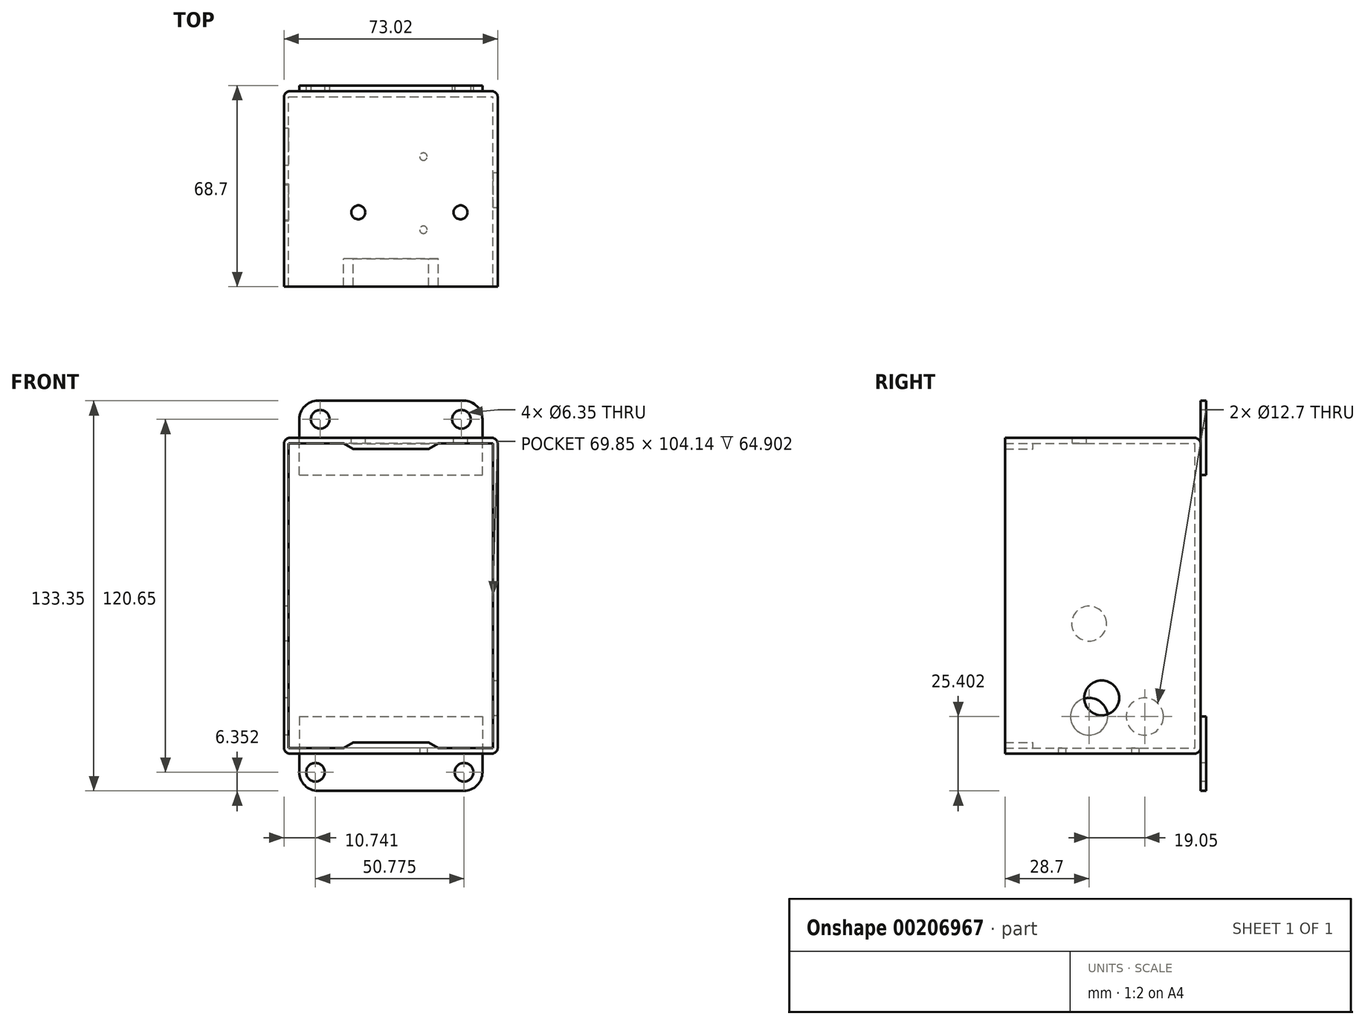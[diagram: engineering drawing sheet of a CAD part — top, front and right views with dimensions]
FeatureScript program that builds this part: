
annotation { "Feature Type Name" : "Feature", "Feature Type Description" : "" }
export const myFeature = defineFeature(function(context is Context, id is Id, definition is map)
    precondition{}
    {
        {
            var Q0;
            Q0=qCreatedBy(makeId("Front.planeOp"),FACE);
            var sketch = newSketch(context, id + "F0", { "sketchPlane" : qUnion([Q0])});
            skLineSegment(sketch, "E0", {"start": v(-80.79, 134.9) * mm, "end": v(-131.65, 134.9) * mm});
            skLineSegment(sketch, "E1", {"start": v(-74.44, 125.38) * mm, "end": v(-74.44, 128.55) * mm});
            skLineSegment(sketch, "E2", {"start": v(-138, 125.38) * mm, "end": v(-138, 128.55) * mm});
            skCircle(sketch, "E3", {"center": v(-81.58, 128.55) * mm, "radius": 3.18 * mm});
            skCircle(sketch, "E4", {"center": v(-130.86, 128.55) * mm, "radius": 3.18 * mm});
            skArc(sketch, "E5", {"start": v(-74.44, 128.55) * mm, "mid": v(-76.3, 133.04) * mm, "end": v(-80.79, 134.9) * mm});
            skArc(sketch, "E6", {"start": v(-131.65, 134.9) * mm, "mid": v(-136.14, 133.04) * mm, "end": v(-138, 128.55) * mm});
            skArc(sketch, "E7", {"start": v(-138, 7.9) * mm, "mid": v(-136.14, 3.41) * mm, "end": v(-131.65, 1.55) * mm});
            skArc(sketch, "E8", {"start": v(-80.79, 1.55) * mm, "mid": v(-76.3, 3.41) * mm, "end": v(-74.44, 7.9) * mm});
            skCircle(sketch, "E9", {"center": v(-130.86, 7.9) * mm, "radius": 3.18 * mm});
            skCircle(sketch, "E10", {"center": v(-81.58, 7.9) * mm, "radius": 3.18 * mm});
            skLineSegment(sketch, "E11", {"start": v(-138, 11.08) * mm, "end": v(-138, 7.9) * mm});
            skLineSegment(sketch, "E12", {"start": v(-74.44, 11.08) * mm, "end": v(-74.44, 7.9) * mm});
            skLineSegment(sketch, "E13", {"start": v(-80.79, 1.55) * mm, "end": v(-131.65, 1.55) * mm});
            skLineSegment(sketch, "E14", {"start": v(-141.97, -160.1) * mm, "end": v(-70.47, -160.1) * mm});
            skLineSegment(sketch, "E15", {"start": v(-141.97, -98.67) * mm, "end": v(-141.97, -160.1) * mm});
            skLineSegment(sketch, "E16", {"start": v(-70.47, -98.67) * mm, "end": v(-70.47, -160.1) * mm});
            skLineSegment(sketch, "E17", {"start": v(-74.44, -160.1) * mm, "end": v(-74.44, -162.01) * mm});
            skLineSegment(sketch, "E18", {"start": v(-138, -160.1) * mm, "end": v(-138, -162.01) * mm});
            skLineSegment(sketch, "E19", {"start": v(-138, -162.01) * mm, "end": v(-74.44, -162.01) * mm});
            skLineSegment(sketch, "E20", {"start": v(-119.33, -98.67) * mm, "end": v(-119.33, -104.55) * mm});
            skLineSegment(sketch, "E21", {"start": v(-93.1, -98.67) * mm, "end": v(-93.1, -104.55) * mm});
            skLineSegment(sketch, "E22", {"start": v(-119.33, -104.55) * mm, "end": v(-93.1, -104.55) * mm});
            skLineSegment(sketch, "E23", {"start": v(-143.69, -89.15) * mm, "end": v(-68.75, -89.15) * mm});
            skLineSegment(sketch, "E24", {"start": v(-145.98, -98.67) * mm, "end": v(-66.46, -98.67) * mm});
            skLineSegment(sketch, "E25", {"start": v(-67.17, -90.6) * mm, "end": v(-66.46, -98.67) * mm});
            skLineSegment(sketch, "E26", {"start": v(-145.27, -90.6) * mm, "end": v(-145.98, -98.67) * mm});
            skArc(sketch, "E27", {"start": v(-67.17, -90.6) * mm, "mid": v(-67.67, -89.57) * mm, "end": v(-68.75, -89.15) * mm});
            skArc(sketch, "E28", {"start": v(-143.69, -89.15) * mm, "mid": v(-144.76, -89.57) * mm, "end": v(-145.27, -90.6) * mm});
            skLineSegment(sketch, "E29", {"start": v(-106.22, -87.6) * mm, "end": v(-105.17, -87.6) * mm});
            skArc(sketch, "E30", {"start": v(-101.46, -89.15) * mm, "mid": v(-103, -87.36) * mm, "end": v(-105.17, -86.4) * mm});
            skLineSegment(sketch, "E31", {"start": v(-105.17, -87.6) * mm, "end": v(-105.17, -86.4) * mm});
            skLineSegment(sketch, "E32", {"start": v(-106.22, -87.6) * mm, "end": v(-107.27, -87.6) * mm});
            skLineSegment(sketch, "E33", {"start": v(-107.27, -87.6) * mm, "end": v(-107.27, -86.4) * mm});
            skArc(sketch, "E34", {"start": v(-107.27, -86.4) * mm, "mid": v(-109.43, -87.36) * mm, "end": v(-110.98, -89.15) * mm});
            skLineSegment(sketch, "E35", {"start": v(-66.46, 14.25) * mm, "end": v(-66.46, 122.2) * mm});
            skLineSegment(sketch, "E36", {"start": v(-145.98, 14.25) * mm, "end": v(-145.98, 122.2) * mm});
            skLineSegment(sketch, "E37", {"start": v(-69.63, 125.38) * mm, "end": v(-142.8, 125.38) * mm});
            skLineSegment(sketch, "E38", {"start": v(-69.63, 11.08) * mm, "end": v(-142.8, 11.08) * mm});
            skArc(sketch, "E39", {"start": v(6.1, 134.9) * mm, "mid": v(1.6, 133.04) * mm, "end": v(-0.25, 128.55) * mm});
            skArc(sketch, "E40", {"start": v(62.3, 128.55) * mm, "mid": v(60.43, 133.04) * mm, "end": v(55.94, 134.9) * mm});
            skCircle(sketch, "E41", {"center": v(6.89, 128.55) * mm, "radius": 3.18 * mm});
            skCircle(sketch, "E42", {"center": v(55.15, 128.55) * mm, "radius": 3.18 * mm});
            skLineSegment(sketch, "E43", {"start": v(55.94, 1.55) * mm, "end": v(6.1, 1.55) * mm});
            skLineSegment(sketch, "E44", {"start": v(67.53, 14.25) * mm, "end": v(62.3, 14.25) * mm});
            skLineSegment(sketch, "E45", {"start": v(65.94, 16.16) * mm, "end": v(47.21, 16.16) * mm});
            skLineSegment(sketch, "E46", {"start": v(65.94, 120.3) * mm, "end": v(47.21, 120.3) * mm});
            skLineSegment(sketch, "E47", {"start": v(-5.5, 14.25) * mm, "end": v(-5.5, 122.2) * mm});
            skLineSegment(sketch, "E48", {"start": v(-3.9, 16.16) * mm, "end": v(-3.9, 120.3) * mm});
            skCircle(sketch, "E49", {"center": v(5.25, 7.9) * mm, "radius": 3.18 * mm});
            skArc(sketch, "E50", {"start": v(-0.25, 7.9) * mm, "mid": v(1.6, 3.41) * mm, "end": v(6.1, 1.55) * mm});
            skLineSegment(sketch, "E51", {"start": v(-3.9, 16.16) * mm, "end": v(14.83, 16.16) * mm});
            skLineSegment(sketch, "E52", {"start": v(-5.5, 14.25) * mm, "end": v(-0.25, 14.25) * mm});
            skLineSegment(sketch, "E53", {"start": v(-0.25, 14.25) * mm, "end": v(-0.25, 7.9) * mm});
            skLineSegment(sketch, "E54", {"start": v(14.83, 16.16) * mm, "end": v(18.13, 18.06) * mm});
            skLineSegment(sketch, "E55", {"start": v(-0.25, 14.25) * mm, "end": v(62.3, 14.25) * mm});
            skLineSegment(sketch, "E56", {"start": v(18.13, 18.06) * mm, "end": v(43.91, 18.06) * mm});
            skLineSegment(sketch, "E57", {"start": v(47.21, 16.16) * mm, "end": v(43.91, 18.06) * mm});
            skLineSegment(sketch, "E58", {"start": v(62.3, 122.2) * mm, "end": v(67.53, 122.2) * mm});
            skLineSegment(sketch, "E59", {"start": v(-3.9, 120.3) * mm, "end": v(14.83, 120.3) * mm});
            skLineSegment(sketch, "E60", {"start": v(-0.25, 122.2) * mm, "end": v(-0.25, 128.55) * mm});
            skLineSegment(sketch, "E61", {"start": v(14.83, 120.3) * mm, "end": v(18.13, 118.4) * mm});
            skLineSegment(sketch, "E62", {"start": v(18.13, 118.4) * mm, "end": v(43.91, 118.4) * mm});
            skLineSegment(sketch, "E63", {"start": v(47.21, 120.3) * mm, "end": v(43.91, 118.4) * mm});
            skLineSegment(sketch, "E64", {"start": v(67.53, 122.2) * mm, "end": v(67.53, 14.25) * mm});
            skLineSegment(sketch, "E65", {"start": v(65.94, 120.3) * mm, "end": v(65.94, 16.16) * mm});
            skArc(sketch, "E66", {"start": v(55.94, 1.55) * mm, "mid": v(60.43, 3.41) * mm, "end": v(62.3, 7.9) * mm});
            skLineSegment(sketch, "E67", {"start": v(62.3, 14.25) * mm, "end": v(62.3, 7.9) * mm});
            skCircle(sketch, "E68", {"center": v(56.03, 7.9) * mm, "radius": 3.18 * mm});
            skLineSegment(sketch, "E69", {"start": v(62.3, 122.2) * mm, "end": v(62.3, 128.55) * mm});
            skLineSegment(sketch, "E70", {"start": v(55.94, 134.9) * mm, "end": v(6.1, 134.9) * mm});
            skCircle(sketch, "E71", {"center": v(-106.22, 119.28) * mm, "radius": 4.76 * mm});
            skCircle(sketch, "E72", {"center": v(-106.22, 18.19) * mm, "radius": 4.76 * mm});
            skLineSegment(sketch, "E73", {"start": v(-105.17, 13.54) * mm, "end": v(-105.17, 22.83) * mm});
            skLineSegment(sketch, "E74", {"start": v(-107.27, 13.54) * mm, "end": v(-107.27, 22.83) * mm});
            skLineSegment(sketch, "E75", {"start": v(-110.49, 121.4) * mm, "end": v(-103.27, 115.54) * mm});
            skLineSegment(sketch, "E76", {"start": v(-109.17, 123.02) * mm, "end": v(-101.95, 117.17) * mm});
            skArc(sketch, "E77", {"start": v(-66.46, 122.2) * mm, "mid": v(-67.39, 124.45) * mm, "end": v(-69.63, 125.38) * mm});
            skArc(sketch, "E78", {"start": v(-142.8, 125.38) * mm, "mid": v(-145.05, 124.45) * mm, "end": v(-145.98, 122.2) * mm});
            skArc(sketch, "E79", {"start": v(-145.98, 14.25) * mm, "mid": v(-145.05, 12) * mm, "end": v(-142.8, 11.08) * mm});
            skArc(sketch, "E80", {"start": v(-69.63, 11.08) * mm, "mid": v(-67.39, 12) * mm, "end": v(-66.46, 14.25) * mm});
            skLineSegment(sketch, "E81", {"start": v(-141.97, -93.43) * mm, "end": v(-70.47, -93.43) * mm});
            skLineSegment(sketch, "E82", {"start": v(-141.97, -93.43) * mm, "end": v(-141.97, -98.67) * mm});
            skLineSegment(sketch, "E83", {"start": v(-70.47, -98.67) * mm, "end": v(-70.47, -93.43) * mm});
            skLineSegment(sketch, "E84", {"start": v(-72.37, -98.67) * mm, "end": v(-72.37, -158.2) * mm});
            skLineSegment(sketch, "E85", {"start": v(-140.06, -158.2) * mm, "end": v(-72.37, -158.2) * mm});
            skLineSegment(sketch, "E86", {"start": v(-140.06, -98.67) * mm, "end": v(-140.06, -158.2) * mm});
            skLineSegment(sketch, "E87", {"start": v(-140.06, -93.43) * mm, "end": v(-140.06, -98.67) * mm});
            skLineSegment(sketch, "E88", {"start": v(-72.37, -98.67) * mm, "end": v(-72.37, -93.43) * mm});
            skLineSegment(sketch, "E89", {"start": v(-86.66, 128.55) * mm, "end": v(-76.5, 128.55) * mm});
            skLineSegment(sketch, "E90", {"start": v(-81.58, 133.63) * mm, "end": v(-81.58, 123.47) * mm});
            skLineSegment(sketch, "E91", {"start": v(-135.94, 128.55) * mm, "end": v(-125.78, 128.55) * mm});
            skLineSegment(sketch, "E92", {"start": v(-130.86, 133.63) * mm, "end": v(-130.86, 123.47) * mm});
            skLineSegment(sketch, "E93", {"start": v(-135.94, 7.9) * mm, "end": v(-125.78, 7.9) * mm});
            skLineSegment(sketch, "E94", {"start": v(-130.86, 12.98) * mm, "end": v(-130.86, 2.82) * mm});
            skLineSegment(sketch, "E95", {"start": v(-86.66, 7.9) * mm, "end": v(-76.5, 7.9) * mm});
            skLineSegment(sketch, "E96", {"start": v(-81.58, 12.98) * mm, "end": v(-81.58, 2.82) * mm});
            skLineSegment(sketch, "E97", {"start": v(0.17, 7.9) * mm, "end": v(10.33, 7.9) * mm});
            skLineSegment(sketch, "E98", {"start": v(5.25, 12.98) * mm, "end": v(5.25, 2.82) * mm});
            skLineSegment(sketch, "E99", {"start": v(50.95, 7.9) * mm, "end": v(61.1, 7.9) * mm});
            skLineSegment(sketch, "E100", {"start": v(56.03, 12.98) * mm, "end": v(56.03, 2.82) * mm});
            skLineSegment(sketch, "E101", {"start": v(50.07, 128.55) * mm, "end": v(60.23, 128.55) * mm});
            skLineSegment(sketch, "E102", {"start": v(55.15, 133.63) * mm, "end": v(55.15, 123.47) * mm});
            skLineSegment(sketch, "E103", {"start": v(1.8, 128.55) * mm, "end": v(11.97, 128.55) * mm});
            skLineSegment(sketch, "E104", {"start": v(6.89, 133.63) * mm, "end": v(6.89, 123.47) * mm});
            skLineSegment(sketch, "E105", {"start": v(-134.03, -160.1) * mm, "end": v(-134.03, -162.01) * mm});
            skLineSegment(sketch, "E106", {"start": v(-127.68, -160.1) * mm, "end": v(-127.68, -162.01) * mm});
            skLineSegment(sketch, "E107", {"start": v(-78.4, -160.1) * mm, "end": v(-78.4, -162.01) * mm});
            skLineSegment(sketch, "E108", {"start": v(-84.76, -160.1) * mm, "end": v(-84.76, -162.01) * mm});
            skLineSegment(sketch, "E109", {"start": v(-130.86, -166.2) * mm, "end": v(-130.86, -155.92) * mm});
            skLineSegment(sketch, "E110", {"start": v(-81.58, -166.2) * mm, "end": v(-81.58, -155.92) * mm});
            skLineSegment(sketch, "E111", {"start": v(-0.25, 122.2) * mm, "end": v(-5.5, 122.2) * mm});
            skLineSegment(sketch, "E112", {"start": v(-0.25, 122.2) * mm, "end": v(62.3, 122.2) * mm});
            skSolve(sketch);
        }
        {
            var Q0;
            Q0=makeQuery(id+"F0.imprint","IMPRINT",FACE,{"disambiguationData":[TD([[makeQuery(id+"F0.imprint","IMPRINT",EDGE,{"derivedFrom":sQuery(id+"F0.wireOp",EDGE,"E44")}),-1.0]])]});
            extrude(context, id + "F1", {"entities" : qUnion([Q0]), "depth" : 66.8 * mm});
        }
        {
            var Q0;
            Q0=makeQuery(id+"F0.imprint","IMPRINT",FACE,{"disambiguationData":[TD([[makeQuery(id+"F0.imprint","IMPRINT",EDGE,{"derivedFrom":sQuery(id+"F0.wireOp",EDGE,"E43")}),-1.0]])]});
            var Q1;
            Q1=makeQuery(id+"F0.imprint","IMPRINT",FACE,{"disambiguationData":[TD([[makeQuery(id+"F0.imprint","IMPRINT",EDGE,{"derivedFrom":sQuery(id+"F0.wireOp",EDGE,"E39")}),1.0]])]});
            var Q2;
            Q2=sQuery(id+"F0.wireOp",EDGE,"E55");
            var Q3;
            Q3=sQuery(id+"F0.wireOp",EDGE,"E53");
            var Q4;
            Q4=sQuery(id+"F0.wireOp",EDGE,"E50");
            var Q5;
            Q5=sQuery(id+"F0.wireOp",EDGE,"E43");
            var Q6;
            Q6=sQuery(id+"F0.wireOp",EDGE,"E67");
            var Q7;
            Q7=sQuery(id+"F0.wireOp",EDGE,"E66");
            extrude(context, id + "F2", {"entities" : qUnion([Q0, Q1]), "surfaceEntities" : qUnion([Q2, Q3, Q4, Q5, Q6, Q7]), "oppositeDirection" : true, "depth" : 1.9 * mm});
        }
        {
            var Q0;
            Q0=makeQuery(id+"F0.imprint","IMPRINT",FACE,{"disambiguationData":[TD([[makeQuery(id+"F0.imprint","IMPRINT",EDGE,{"derivedFrom":sQuery(id+"F0.wireOp",EDGE,"E45")}),-1.0]])]});
            var Q1;
            Q1=sQuery(id+"F0.wireOp",EDGE,"E65");
            var Q2;
            Q2=sQuery(id+"F0.wireOp",EDGE,"E46");
            var Q3;
            Q3=sQuery(id+"F0.wireOp",EDGE,"E63");
            var Q4;
            Q4=sQuery(id+"F0.wireOp",EDGE,"E62");
            var Q5;
            Q5=sQuery(id+"F0.wireOp",EDGE,"E61");
            var Q6;
            Q6=sQuery(id+"F0.wireOp",EDGE,"E59");
            var Q7;
            Q7=sQuery(id+"F0.wireOp",EDGE,"E48");
            var Q8;
            Q8=sQuery(id+"F0.wireOp",EDGE,"E45");
            var Q9;
            Q9=sQuery(id+"F0.wireOp",EDGE,"E57");
            var Q10;
            Q10=sQuery(id+"F0.wireOp",EDGE,"E56");
            var Q11;
            Q11=sQuery(id+"F0.wireOp",EDGE,"E54");
            var Q12;
            Q12=sQuery(id+"F0.wireOp",EDGE,"E51");
            extrude(context, id + "F3", {"entities" : qUnion([Q0]), "operationType" : NewBodyOperationType.ADD, "surfaceEntities" : qUnion([Q1, Q2, Q3, Q4, Q5, Q6, Q7, Q8, Q9, Q10, Q11, Q12]), "depth" : 1.9 * mm});
        }
        {
            var Q0;
            Q0=makeQuery(id+"F1.opExtrude","SWEPT_EDGE",EDGE,{"disambiguationData":[OSD([sQuery(id+"F0.wireOp",EDGE,"E47"),sQuery(id+"F0.wireOp",EDGE,"E111")])]});
            var Q1;
            Q1=makeQuery(id+"F1.opExtrude","SWEPT_EDGE",EDGE,{"disambiguationData":[OSD([sQuery(id+"F0.wireOp",EDGE,"E58"),sQuery(id+"F0.wireOp",EDGE,"E64")])]});
            var Q2;
            Q2=makeQuery(id+"F1.opExtrude","SWEPT_EDGE",EDGE,{"disambiguationData":[OSD([sQuery(id+"F0.wireOp",EDGE,"E44"),sQuery(id+"F0.wireOp",EDGE,"E64")])]});
            var Q3;
            Q3=makeQuery(id+"F1.opExtrude","SWEPT_EDGE",EDGE,{"disambiguationData":[OSD([sQuery(id+"F0.wireOp",EDGE,"E47"),sQuery(id+"F0.wireOp",EDGE,"E52")])]});
            var Q4;
            Q4=makeQuery(id+"F1.opExtrude","CAP_EDGE",EDGE,{"disambiguationData":[OSD([sQuery(id+"F0.wireOp",EDGE,"E47")])],"isStart":true});
            var Q5;
            Q5=makeQuery(id+"F1.opExtrude","CAP_EDGE",EDGE,{"disambiguationData":[OSD([sQuery(id+"F0.wireOp",EDGE,"E64")])],"isStart":true});
            var Q6;
            Q6=makeQuery(id+"F1.opExtrude","CAP_EDGE",EDGE,{"disambiguationData":[OSD([sQuery(id+"F0.wireOp",EDGE,"E58"),sQuery(id+"F0.wireOp",EDGE,"E111"),sQuery(id+"F0.wireOp",EDGE,"E112")])],"isStart":true});
            var Q7;
            Q7=makeQuery(id+"F1.opExtrude","CAP_EDGE",EDGE,{"disambiguationData":[OSD([sQuery(id+"F0.wireOp",EDGE,"E44"),sQuery(id+"F0.wireOp",EDGE,"E52"),sQuery(id+"F0.wireOp",EDGE,"E55")])],"isStart":true});
            fillet(context, id + "F4", {"entities" : qUnion([Q0, Q1, Q2, Q3, Q4, Q5, Q6, Q7]), "radius" : 2.03 * mm, "tangentPropagation" : true, "allowEdgeOverflow" : false});
        }
        {
            var Q0;
            Q0=makeQuery(id+"F2.opExtrude","SWEPT_FACE",FACE,{"disambiguationData":[OSD([sQuery(id+"F0.wireOp",EDGE,"E55")])]});
            extrude(context, id + "F5", {"entities" : qUnion([Q0]), "operationType" : NewBodyOperationType.ADD, "depth" : 12.7 * mm});
        }
        {
            var Q0;
            Q0=makeQuery(id+"F2.opExtrude","SWEPT_FACE",FACE,{"disambiguationData":[OSD([sQuery(id+"F0.wireOp",EDGE,"E112")])]});
            extrude(context, id + "F6", {"entities" : qUnion([Q0]), "operationType" : NewBodyOperationType.ADD, "depth" : 12.7 * mm});
        }
        {
            var Q0;
            Q0=makeQuery(id+"F1.opExtrude","SWEPT_FACE",FACE,{"disambiguationData":[OSD([sQuery(id+"F0.wireOp",EDGE,"E47")])]});
            var sketch = newSketch(context, id + "F7", { "sketchPlane" : qUnion([Q0])});
            skCircle(sketch, "E113", {"center": v(38.1, 26.95) * mm, "radius": 6.35 * mm});
            skCircle(sketch, "E114", {"center": v(19.05, 26.95) * mm, "radius": 6.35 * mm});
            skSolve(sketch);
        }
        {
            var Q0;
            Q0=qSketchRegion(id+"F7",true);
            extrude(context, id + "F8", {"entities" : qUnion([Q0]), "operationType" : NewBodyOperationType.REMOVE, "endBound" : BoundingType.UP_TO_NEXT, "oppositeDirection" : true, "depth" : 25.4 * mm});
        }
        {
            var Q0;
            Q0=makeQuery(id+"F1.opExtrude","SWEPT_FACE",FACE,{"disambiguationData":[OSD([sQuery(id+"F0.wireOp",EDGE,"E44"),sQuery(id+"F0.wireOp",EDGE,"E52"),sQuery(id+"F0.wireOp",EDGE,"E55")])]});
            var sketch = newSketch(context, id + "F9", { "sketchPlane" : qUnion([Q0])});
            skCircle(sketch, "E115", {"center": v(42.13, 47.35) * mm, "radius": 1.27 * mm});
            skCircle(sketch, "E116", {"center": v(42.13, 22.35) * mm, "radius": 1.27 * mm});
            skSolve(sketch);
        }
        {
            var Q0;
            Q0=qSketchRegion(id+"F9",true);
            extrude(context, id + "F10", {"entities" : qUnion([Q0]), "operationType" : NewBodyOperationType.REMOVE, "endBound" : BoundingType.UP_TO_NEXT, "oppositeDirection" : true, "depth" : 25.4 * mm});
        }
        {
            var Q0;
            Q0=makeQuery(id+"F1.opExtrude","SWEPT_FACE",FACE,{"disambiguationData":[OSD([sQuery(id+"F0.wireOp",EDGE,"E62")])]});
            var sketch = newSketch(context, id + "F11", { "sketchPlane" : qUnion([Q0])});
            skLineSegment(sketch, "E117.bottom", {"start": v(11.05, 57.23) * mm, "end": v(54.23, 57.23) * mm});
            skLineSegment(sketch, "E117.top", {"start": v(11.05, 1.9) * mm, "end": v(54.23, 1.9) * mm});
            skLineSegment(sketch, "E117.left", {"start": v(11.05, 57.23) * mm, "end": v(11.05, 1.9) * mm});
            skLineSegment(sketch, "E117.right", {"start": v(54.23, 57.23) * mm, "end": v(54.23, 1.9) * mm});
            skSolve(sketch);
        }
        {
            var Q0;
            Q0=qSketchRegion(id+"F11",true);
            var Q1;
            Q1=makeQuery(id+"F1.opExtrude","SWEPT_FACE",FACE,{"disambiguationData":[OSD([sQuery(id+"F0.wireOp",EDGE,"E51")])]});
            var Q2;
            Q2=makeQuery(id+"F1.opExtrude","SWEPT_FACE",FACE,{"disambiguationData":[OSD([sQuery(id+"F0.wireOp",EDGE,"E46")])]});
            extrude(context, id + "F12", {"entities" : qUnion([Q0, Q1]), "operationType" : NewBodyOperationType.REMOVE, "endBound" : BoundingType.UP_TO_SURFACE, "oppositeDirection" : true, "endBoundEntityFace" : qUnion([Q2]), "depth" : 25.4 * mm});
        }
        {
            var Q0;
            Q0=makeQuery(id+"F1.opExtrude","SWEPT_FACE",FACE,{"disambiguationData":[OSD([sQuery(id+"F0.wireOp",EDGE,"E56")])]});
            var sketch = newSketch(context, id + "F13", { "sketchPlane" : qUnion([Q0])});
            skLineSegment(sketch, "E118.bottom", {"start": v(8.8, -1.9) * mm, "end": v(51.97, -1.9) * mm});
            skLineSegment(sketch, "E118.top", {"start": v(8.8, -57.23) * mm, "end": v(51.97, -57.23) * mm});
            skLineSegment(sketch, "E118.left", {"start": v(8.8, -1.9) * mm, "end": v(8.8, -57.23) * mm});
            skLineSegment(sketch, "E118.right", {"start": v(51.97, -1.9) * mm, "end": v(51.97, -57.23) * mm});
            skSolve(sketch);
        }
        {
            var Q0;
            Q0=qSketchRegion(id+"F13",true);
            var Q1;
            Q1=makeQuery(id+"F1.opExtrude","SWEPT_FACE",FACE,{"disambiguationData":[OSD([sQuery(id+"F0.wireOp",EDGE,"E51")])]});
            extrude(context, id + "F14", {"entities" : qUnion([Q0]), "operationType" : NewBodyOperationType.REMOVE, "endBound" : BoundingType.UP_TO_SURFACE, "oppositeDirection" : true, "endBoundEntityFace" : qUnion([Q1]), "depth" : 25.4 * mm});
        }
        {
            var Q0;
            Q0=makeQuery(id+"F1.opExtrude","SWEPT_FACE",FACE,{"disambiguationData":[OSD([sQuery(id+"F0.wireOp",EDGE,"E58"),sQuery(id+"F0.wireOp",EDGE,"E111"),sQuery(id+"F0.wireOp",EDGE,"E112")])]});
            var sketch = newSketch(context, id + "F15", { "sketchPlane" : qUnion([Q0])});
            skCircle(sketch, "E119", {"center": v(19.9, -41.4) * mm, "radius": 2.37 * mm});
            skCircle(sketch, "E120", {"center": v(54.83, -41.4) * mm, "radius": 2.37 * mm});
            skSolve(sketch);
        }
        {
            var Q0;
            Q0=qSketchRegion(id+"F15",true);
            extrude(context, id + "F16", {"entities" : qUnion([Q0]), "operationType" : NewBodyOperationType.REMOVE, "endBound" : BoundingType.UP_TO_NEXT, "oppositeDirection" : true, "depth" : 25.4 * mm});
        }
        {
            var Q0;
            Q0=makeQuery(id+"F1.opExtrude","SWEPT_FACE",FACE,{"disambiguationData":[OSD([sQuery(id+"F0.wireOp",EDGE,"E64")])]});
            var sketch = newSketch(context, id + "F17", { "sketchPlane" : qUnion([Q0])});
            skCircle(sketch, "E121", {"center": v(-33.78, 33.3) * mm, "radius": 5.97 * mm});
            skSolve(sketch);
        }
        {
            var Q0;
            Q0=qSketchRegion(id+"F17",true);
            extrude(context, id + "F18", {"entities" : qUnion([Q0]), "operationType" : NewBodyOperationType.REMOVE, "endBound" : BoundingType.UP_TO_NEXT, "oppositeDirection" : true, "depth" : 25.4 * mm});
        }
        {
            var Q0;
            Q0=makeQuery(id+"F1.opExtrude","SWEPT_FACE",FACE,{"disambiguationData":[OSD([sQuery(id+"F0.wireOp",EDGE,"E47")])]});
            var sketch = newSketch(context, id + "F19", { "sketchPlane" : qUnion([Q0])});
            skCircle(sketch, "E122", {"center": v(38.1, 58.7) * mm, "radius": 5.97 * mm});
            skSolve(sketch);
        }
        {
            var Q0;
            Q0=qSketchRegion(id+"F19",true);
            var Q1;
            Q1=makeQuery(id+"F1.opExtrude","SWEPT_FACE",FACE,{"disambiguationData":[OSD([sQuery(id+"F0.wireOp",EDGE,"E48")])]});
            extrude(context, id + "F20", {"entities" : qUnion([Q0]), "operationType" : NewBodyOperationType.REMOVE, "endBound" : BoundingType.UP_TO_SURFACE, "oppositeDirection" : true, "endBoundEntityFace" : qUnion([Q1]), "depth" : 25.4 * mm});
        }
    });
